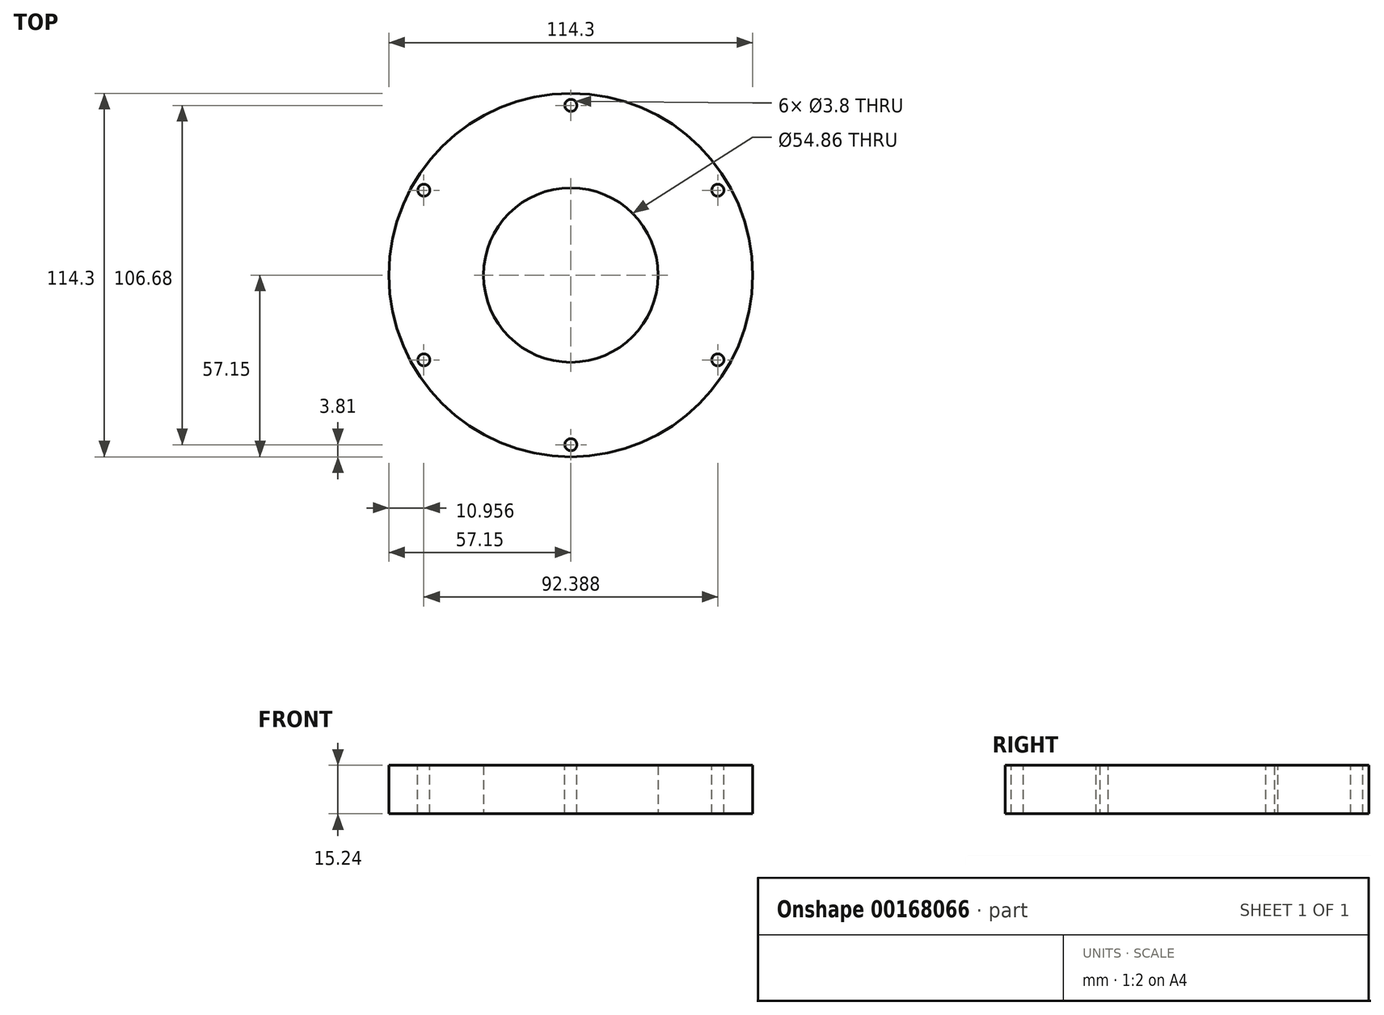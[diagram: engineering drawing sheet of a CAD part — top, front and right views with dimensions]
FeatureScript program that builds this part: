
annotation { "Feature Type Name" : "Feature", "Feature Type Description" : "" }
export const myFeature = defineFeature(function(context is Context, id is Id, definition is map)
    precondition{}
    {
        {
            var Q0;
            Q0=qCreatedBy(makeId("Top.planeOp"),FACE);
            var sketch = newSketch(context, id + "F0", { "sketchPlane" : qUnion([Q0])});
            skCircle(sketch, "E0", {"center": v(0, 0) * mm, "radius": 57.15 * mm});
            skCircle(sketch, "E1", {"center": v(0, 0) * mm, "radius": 27.43 * mm});
            skSolve(sketch);
        }
        {
            var Q0;
            Q0=qSketchRegion(id+"F0",true);
            extrude(context, id + "F1", {"entities" : qUnion([Q0]), "depth" : 15.24 * mm});
        }
        {
            var Q0;
            Q0=makeQuery(id+"F1.opExtrude","CAP_FACE",FACE,{"disambiguationData":[OSD([sQuery(id+"F0.wireOp",EDGE,"E0"),sQuery(id+"F0.wireOp",EDGE,"E1")])],"isStart":false});
            var sketch = newSketch(context, id + "F2", { "sketchPlane" : qUnion([Q0])});
            skLineSegment(sketch, "E2", {"start": v(0, 0) * mm, "end": v(0, -53.34) * mm, "construction": true});
            skPoint(sketch, "E3", {"position": v(0, -53.34) * mm});
            skPoint(sketch, "E4.1.0", {"position": v(46.2, -26.67) * mm});
            skPoint(sketch, "E4.2.0", {"position": v(46.2, 26.67) * mm});
            skPoint(sketch, "E4.3.0", {"position": v(0, 53.34) * mm});
            skPoint(sketch, "E4.4.0", {"position": v(-46.2, 26.67) * mm});
            skPoint(sketch, "E4.5.0", {"position": v(-46.2, -26.67) * mm});
            skPoint(sketch, "E4.center", {"position": v(0, 0) * mm});
            skSolve(sketch);
        }
        {
            var Q0;
            Q0=sQuery(id+"F2.wireOp",VERTEX,"E3");
            var Q1;
            Q1=sQuery(id+"F2.wireOp",VERTEX,"E4.1.0");
            var Q2;
            Q2=sQuery(id+"F2.wireOp",VERTEX,"E4.2.0");
            var Q3;
            Q3=sQuery(id+"F2.wireOp",VERTEX,"E4.3.0");
            var Q4;
            Q4=sQuery(id+"F2.wireOp",VERTEX,"E4.4.0");
            var Q5;
            Q5=sQuery(id+"F2.wireOp",VERTEX,"E4.5.0");
            var Q6;
            Q6=makeQuery(id+"F1.opExtrude","SWEPT_BODY",BODY,{"disambiguationData":[OSD([sQuery(id+"F0.wireOp",EDGE,"E0"),sQuery(id+"F0.wireOp",EDGE,"E1")])]});
            hole(context, id + "F3", {"style" : HoleStyle.SIMPLE, "endStyle" : HoleEndStyle.THROUGH, "standardTappedOrClearance" : lookupTablePath({ "standard" : "ANSI", "fit" : "Normal (ASME)", "size" : "#6", "type" : "Clearance" }), "standardBlindInLast" : lookupTablePath({ "fit" : "Free", "standard" : "ANSI", "size" : "#6", "type" : "Clearance" }), "holeDiameter" : 3.8 * mm, "locations" : qUnion([Q0, Q1, Q2, Q3, Q4, Q5]), "scope" : qUnion([Q6]), "isTappedThrough" : true});
        }
    });
